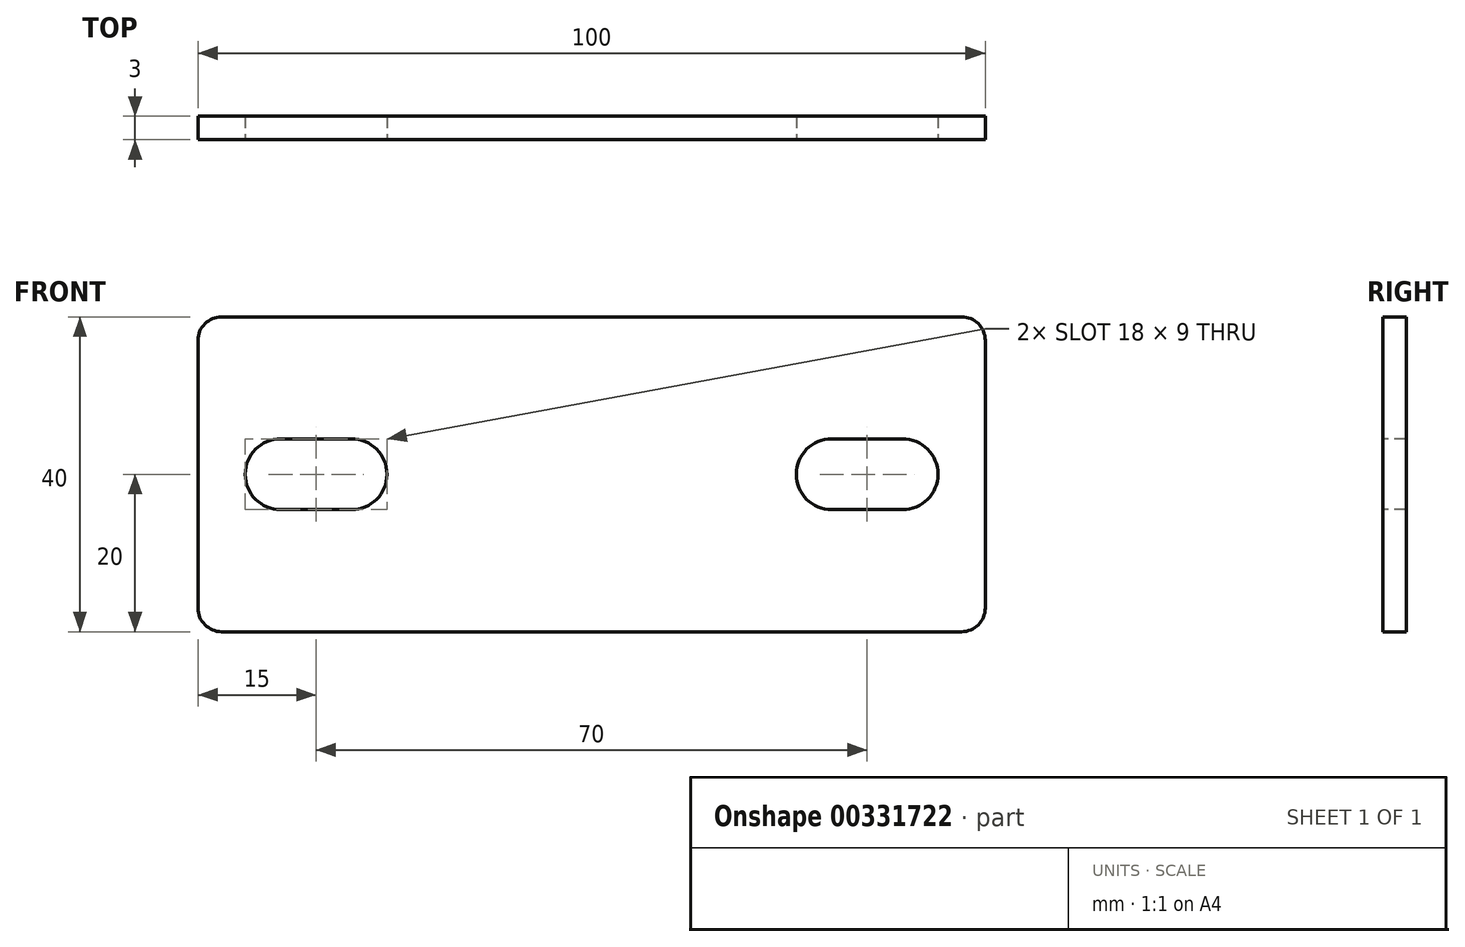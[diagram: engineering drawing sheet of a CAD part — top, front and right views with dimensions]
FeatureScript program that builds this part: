
annotation { "Feature Type Name" : "Feature", "Feature Type Description" : "" }
export const myFeature = defineFeature(function(context is Context, id is Id, definition is map)
    precondition{}
    {
        {
            var Q0;
            Q0=qCreatedBy(makeId("Front.planeOp"),FACE);
            var sketch = newSketch(context, id + "F0", { "sketchPlane" : qUnion([Q0])});
            skLineSegment(sketch, "E0.bottom", {"start": v(50, 20) * mm, "end": v(-50, 20) * mm});
            skLineSegment(sketch, "E0.top", {"start": v(50, -20) * mm, "end": v(-50, -20) * mm});
            skLineSegment(sketch, "E0.left", {"start": v(50, 20) * mm, "end": v(50, -20) * mm});
            skLineSegment(sketch, "E0.right", {"start": v(-50, 20) * mm, "end": v(-50, -20) * mm});
            skPoint(sketch, "E0.middle", {"position": v(0, 0) * mm});
            skSolve(sketch);
        }
        {
            var Q0;
            Q0=makeQuery(id+"F0.imprint","IMPRINT",FACE,{"disambiguationData":[TD([[makeQuery(id+"F0.imprint","IMPRINT",EDGE,{"derivedFrom":sQuery(id+"F0.wireOp",EDGE,"E0.bottom")}),1.0]])]});
            extrude(context, id + "F1", {"entities" : qUnion([Q0]), "depth" : 3 * mm});
        }
        {
            var Q0;
            Q0=makeQuery(id+"F1.opExtrude","CAP_FACE",FACE,{"disambiguationData":[OSD([sQuery(id+"F0.wireOp",EDGE,"E0.bottom"),sQuery(id+"F0.wireOp",EDGE,"E0.top"),sQuery(id+"F0.wireOp",EDGE,"E0.left"),sQuery(id+"F0.wireOp",EDGE,"E0.right")])],"isStart":false});
            var sketch = newSketch(context, id + "F2", { "sketchPlane" : qUnion([Q0])});
            skLineSegment(sketch, "E1.bottom", {"start": v(39.5, 4.5) * mm, "end": v(30.5, 4.5) * mm});
            skLineSegment(sketch, "E1.top", {"start": v(39.5, -4.5) * mm, "end": v(30.5, -4.5) * mm});
            skPoint(sketch, "E1.middle", {"position": v(35, 0) * mm});
            skArc(sketch, "E2", {"start": v(30.5, 4.5) * mm, "mid": v(26, 0) * mm, "end": v(30.5, -4.5) * mm});
            skArc(sketch, "E3", {"start": v(39.5, -4.5) * mm, "mid": v(44, 0) * mm, "end": v(39.5, 4.5) * mm});
            skLineSegment(sketch, "E4.MirrorCS", {"start": v(-39.5, -4.5) * mm, "end": v(-30.5, -4.5) * mm});
            skLineSegment(sketch, "E5.MirrorCS", {"start": v(-39.5, 4.5) * mm, "end": v(-30.5, 4.5) * mm});
            skArc(sketch, "E6.MirrorCS", {"start": v(-39.5, -4.5) * mm, "mid": v(-44, 0) * mm, "end": v(-39.5, 4.5) * mm});
            skArc(sketch, "E7.MirrorCS", {"start": v(-30.5, 4.5) * mm, "mid": v(-26, 0) * mm, "end": v(-30.5, -4.5) * mm});
            skPoint(sketch, "E8.MirrorP", {"position": v(-35, 0) * mm});
            skSolve(sketch);
        }
        {
            var Q0;
            Q0=makeQuery(id+"F2.imprint","IMPRINT",FACE,{"disambiguationData":[TD([[makeQuery(id+"F2.imprint","IMPRINT",EDGE,{"derivedFrom":sQuery(id+"F2.wireOp",EDGE,"E1.bottom")}),1.0]])]});
            var Q1;
            Q1=makeQuery(id+"F2.imprint","IMPRINT",FACE,{"disambiguationData":[TD([[makeQuery(id+"F2.imprint","IMPRINT",EDGE,{"derivedFrom":sQuery(id+"F2.wireOp",EDGE,"E4.MirrorCS")}),1.0]])]});
            extrude(context, id + "F3", {"entities" : qUnion([Q0, Q1]), "operationType" : NewBodyOperationType.REMOVE, "oppositeDirection" : true, "depth" : 25 * mm});
        }
        {
            var Q0;
            Q0=makeQuery(id+"F1.opExtrude","SWEPT_EDGE",EDGE,{"disambiguationData":[OSD([sQuery(id+"F0.wireOp",EDGE,"E0.top"),sQuery(id+"F0.wireOp",EDGE,"E0.left")])]});
            var Q1;
            Q1=makeQuery(id+"F1.opExtrude","SWEPT_EDGE",EDGE,{"disambiguationData":[OSD([sQuery(id+"F0.wireOp",EDGE,"E0.bottom"),sQuery(id+"F0.wireOp",EDGE,"E0.left")])]});
            var Q2;
            Q2=makeQuery(id+"F1.opExtrude","SWEPT_EDGE",EDGE,{"disambiguationData":[OSD([sQuery(id+"F0.wireOp",EDGE,"E0.bottom"),sQuery(id+"F0.wireOp",EDGE,"E0.right")])]});
            var Q3;
            Q3=makeQuery(id+"F1.opExtrude","SWEPT_EDGE",EDGE,{"disambiguationData":[OSD([sQuery(id+"F0.wireOp",EDGE,"E0.top"),sQuery(id+"F0.wireOp",EDGE,"E0.right")])]});
            fillet(context, id + "F4", {"entities" : qUnion([Q0, Q1, Q2, Q3]), "radius" : 3 * mm, "tangentPropagation" : true, "allowEdgeOverflow" : false});
        }
    });
